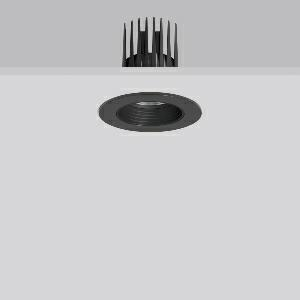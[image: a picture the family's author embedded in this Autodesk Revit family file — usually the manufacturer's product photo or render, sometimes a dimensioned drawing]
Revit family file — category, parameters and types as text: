
# Revit family: heledon_mini_e_901745_003_2_4374
name_source: partatom
category: Lighting Fixtures
units: mm (PartAtom-declared; Revit-internal decimal feet)

## family parameters
Cut with Voids When Loaded = No
Host = Face
Light Source = No
Part Type = Normal
Room Calculation Point = No
Round Connector Dimension = Use Diameter
Shared = No

## types (1)
- HELEDON mini E (1 x LED Modul 927, 1900 lm, 2700)
    Apparent Load = 20 VA
    Approval mark = CE
    CIE Flux Codes = 98 100 100 100 100
    Color Rendering = 92
    Color Temperature = 2700
    Default Elevation = 1800 mm
    Description = Series: HELEDON mini
Round recessed downlight. Housing: die-cast aluminium, powder-coated. Black plastic ring and recessed LED to prevent glare from the side. Optical assembly with lens made of plastic (polycarbonate) for the best homogeneous light distribution - can be changed without tools. Best colour rendering index Ra>90. Suitable for Recessed ceiling mounting. Installation without tools thanks to spring fastening system. Including separate LED converter with connecting cable 600 mm.High quality converter without flickering and stroboscopic effect. Through-wiring box (5 pole) available as accessory. The following accessories can be mounted without use of tools: interchangeable lenses, decorative glasses, honeycomb louvre, clear and frosted diffusers, white interchangeable plastic ring. 
Colour: deep black, matt (RAL 9005)
Diameter: 124 mm
Height: 3 mm
Cut-out diameter: 114 mm
Recess height: 170 mm
Luminaire: recess height: 120 mm
Lamp: LED
Socket: without socket
Colour temperature: 2700K
Colour rendering index (CRI): 92
System power: 20 W
Rated luminous flux: 1900 lm
Luminous efficiency: 95 lm/W
Control gear: Regulated power supply
Protection class: II
Type of protection: IP 20
    Height = 0 mm  [stored 0 ft]
    Lamp = 1 x LED Modul 927
    Lamp Light Flux = 1900 lm
    Lamp count = 1
    Length = 124 mm  [stored 0.406824 ft]
    Lifetime = 50000 h
    Luminous efficacy = 95 lm/W
    Manufacturer = RZB
    ModVariant = No
    Model = 901745.003.2
    Mounting Place = Ceiling
    Mounting Type = Recessed
    Number of Poles = 1
    OnlyDefault = Yes
    Power Factor = 1
    Product Name = HELEDON mini E
    Product group = Recessed downlights
    ProductGroupID = 402
    Protection Class = Protection class II
    Protection Degree = IP 20
    RLX_Detail_Level = 1
    RLX_Emergency_Light_Flux = 0 lm
    RLX_Emergency_Type = 0
    RLX_Emergency_Type_DB = No
    RlxData = <blob elided: 127821 chars, md5=ac3044d8>
    Socket = socket
    Standby Power = 0 W
    System Light Flux = 1900 lm
    System Power = 20 W
    Type Comments = Product without accessories
    Type Image = 901656.003.jpg
    URL = http://relux.com
    VarID = ---
    Voltage = 230 V
    Voltage Range = 220-240 V
    Weight = 0.00 kg
    Width = 0 mm  [stored 0 ft]

note: [stored X ft] marks values corroborated as IEEE doubles in the binary element streams (Revit-internal decimal feet)

## geometry (parser evidence)
native form markers: Blend x4, Sweep x11
no freeform markers — native parametric forms only
